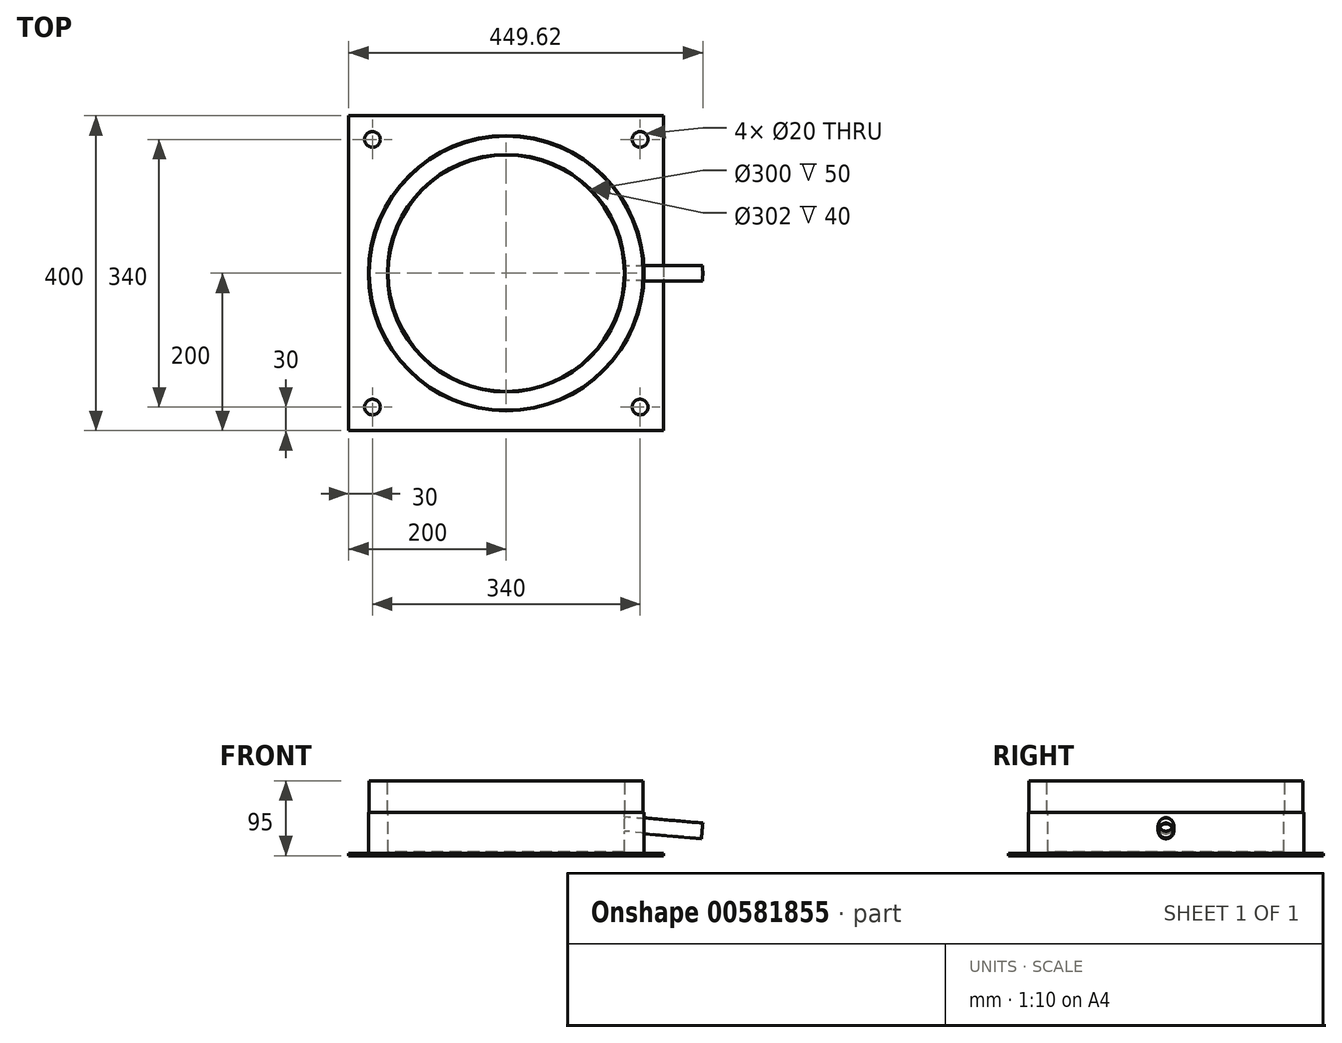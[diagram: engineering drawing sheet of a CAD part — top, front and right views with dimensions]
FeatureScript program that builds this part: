
annotation { "Feature Type Name" : "Feature", "Feature Type Description" : "" }
export const myFeature = defineFeature(function(context is Context, id is Id, definition is map)
    precondition{}
    {
        {
            var Q0;
            Q0=qCreatedBy(makeId("Front.planeOp"),FACE);
            var sketch = newSketch(context, id + "F0", { "sketchPlane" : qUnion([Q0])});
            skLineSegment(sketch, "E0", {"start": v(0, 74.87) * mm, "end": v(0, -73.71) * mm, "construction": true});
            skLineSegment(sketch, "E1", {"start": v(0, 374.84) * mm, "end": v(0, 1) * mm, "construction": true});
            skLineSegment(sketch, "E2", {"start": v(-150, 5) * mm, "end": v(-150, 55) * mm});
            skLineSegment(sketch, "E3", {"start": v(-150, 55) * mm, "end": v(-151, 55) * mm});
            skLineSegment(sketch, "E4", {"start": v(-151, 55) * mm, "end": v(-151, 95) * mm});
            skLineSegment(sketch, "E5", {"start": v(-151, 95) * mm, "end": v(-174, 95) * mm});
            skLineSegment(sketch, "E6", {"start": v(-174, 95) * mm, "end": v(-174, 55) * mm});
            skLineSegment(sketch, "E7", {"start": v(-174, 55) * mm, "end": v(-175, 55) * mm});
            skLineSegment(sketch, "E8", {"start": v(-175, 55) * mm, "end": v(-175, 5) * mm});
            skLineSegment(sketch, "E9", {"start": v(-175, 5) * mm, "end": v(-150, 5) * mm});
            skLineSegment(sketch, "E10.trimOffspring", {"start": v(0, 0) * mm, "end": v(0, -528.94) * mm, "construction": true});
            skLineSegment(sketch, "E11.bottom", {"start": v(-175, 5) * mm, "end": v(-10, 5) * mm});
            skLineSegment(sketch, "E11.top", {"start": v(-175, 2) * mm, "end": v(-10, 2) * mm});
            skLineSegment(sketch, "E11.left", {"start": v(-175, 5) * mm, "end": v(-175, 2) * mm});
            skLineSegment(sketch, "E11.right", {"start": v(-10, 5) * mm, "end": v(-10, 2) * mm});
            skLineSegment(sketch, "E12.bottom", {"start": v(-10, 5) * mm, "end": v(0, 5) * mm});
            skLineSegment(sketch, "E12.top", {"start": v(-10, 2) * mm, "end": v(0, 2) * mm});
            skLineSegment(sketch, "E12.right", {"start": v(0, 5) * mm, "end": v(0, 2) * mm});
            skSolve(sketch);
        }
        {
            var Q0;
            Q0=qSketchRegion(id+"F0",true);
            var Q1;
            Q1=sQuery(id+"F0.wireOp",EDGE,"E1");
            revolve(context, id + "F1", {"entities" : qUnion([Q0]), "axis" : qUnion([Q1]), "revolveType" : RevolveType.FULL});
        }
        {
            var Q0;
            Q0=qCreatedBy(makeId("Top.planeOp"),FACE);
            var sketch = newSketch(context, id + "F2", { "sketchPlane" : qUnion([Q0])});
            skLineSegment(sketch, "E13.bottom", {"start": v(200, 200) * mm, "end": v(-200, 200) * mm});
            skLineSegment(sketch, "E13.top", {"start": v(200, -200) * mm, "end": v(-200, -200) * mm});
            skLineSegment(sketch, "E13.left", {"start": v(200, 200) * mm, "end": v(200, -200) * mm});
            skLineSegment(sketch, "E13.right", {"start": v(-200, 200) * mm, "end": v(-200, -200) * mm});
            skPoint(sketch, "E13.middle", {"position": v(0, 0) * mm});
            skLineSegment(sketch, "E14", {"start": v(0, 0) * mm, "end": v(0, 773.78) * mm, "construction": true});
            skLineSegment(sketch, "E15", {"start": v(0, 0) * mm, "end": v(1007.48, 0) * mm, "construction": true});
            skCircle(sketch, "E16", {"center": v(170, 170) * mm, "radius": 10 * mm});
            skCircle(sketch, "E17.MirrorC", {"center": v(-170, 170) * mm, "radius": 10 * mm});
            skCircle(sketch, "E18.MirrorC", {"center": v(170, -170) * mm, "radius": 10 * mm});
            skCircle(sketch, "E19.MirrorC", {"center": v(-170, -170) * mm, "radius": 10 * mm});
            skSolve(sketch);
        }
        {
            var Q0;
            Q0=qSketchRegion(id+"F2",true);
            extrude(context, id + "F3", {"entities" : qUnion([Q0]), "operationType" : NewBodyOperationType.ADD, "depth" : 3 * mm, "offsetDistance" : 25 * mm});
        }
        {
            var Q0;
            Q0=qCreatedBy(makeId("Front.planeOp"),FACE);
            var sketch = newSketch(context, id + "F4", { "sketchPlane" : qUnion([Q0])});
            skLineSegment(sketch, "E20", {"start": v(175, 38) * mm, "end": v(350.49, 22.65) * mm, "construction": true});
            skLineSegment(sketch, "E21", {"start": v(175, 55) * mm, "end": v(175, 3) * mm, "construction": true});
            skLineSegment(sketch, "E22", {"start": v(150, 50.23) * mm, "end": v(249.62, 41.5) * mm});
            skLineSegment(sketch, "E23", {"start": v(150, 50.23) * mm, "end": v(149.91, 49.23) * mm});
            skLineSegment(sketch, "E24", {"start": v(149.91, 49.23) * mm, "end": v(249.53, 40.51) * mm});
            skLineSegment(sketch, "E25", {"start": v(249.53, 40.51) * mm, "end": v(249.62, 41.5) * mm});
            skSolve(sketch);
        }
        {
            var Q0;
            Q0 = qSketchRegion(id + "F4", true);
            var Q1;
            Q1=sQuery(id+"F4.wireOp",EDGE,"E20");
            revolve(context, id + "F5", {"operationType" : NewBodyOperationType.ADD, "surfaceOperationType" : NewSurfaceOperationType.NEW, "entities" : qUnion([Q0]), "axis" : qUnion([Q1]), "revolveType" : RevolveType.FULL});
        }
        {
            var Q0;
            Q0=makeQuery(id+"F5.opRevolve","SWEPT_FACE",FACE,{"disambiguationData":[OSD([sQuery(id+"F4.wireOp",EDGE,"E25")])]});
            var sketch = newSketch(context, id + "F6", { "sketchPlane" : qUnion([Q0])});
            skCircle(sketch, "E26.0", {"center": v(0, 53.1) * mm, "radius": 9 * mm});
            skSolve(sketch);
        }
        {
            var Q0;
            Q0 = qSketchRegion(id + "F6", true);
            extrude(context, id + "F7", {"entities" : qUnion([Q0]), "operationType" : NewBodyOperationType.REMOVE, "oppositeDirection" : true, "depth" : 120 * mm, "offsetDistance" : 25 * mm});
        }
        {
            var Q0;
            Q0=makeQuery(id+"F1.opRevolve","SWEPT_FACE",FACE,{"disambiguationData":[OSD([sQuery(id+"F0.wireOp",EDGE,"E11.bottom"),sQuery(id+"F0.wireOp",EDGE,"E12.bottom")])]});
            var sketch = newSketch(context, id + "F8", { "sketchPlane" : qUnion([Q0])});
            skCircle(sketch, "E27.0", {"center": v(0, 0) * mm, "radius": 150 * mm});
            skSolve(sketch);
        }
        {
            var Q0;
            Q0 = qSketchRegion(id + "F8", true);
            extrude(context, id + "F9", {"entities" : qUnion([Q0]), "operationType" : NewBodyOperationType.REMOVE, "depth" : 200 * mm, "offsetDistance" : 25 * mm});
        }
    });
